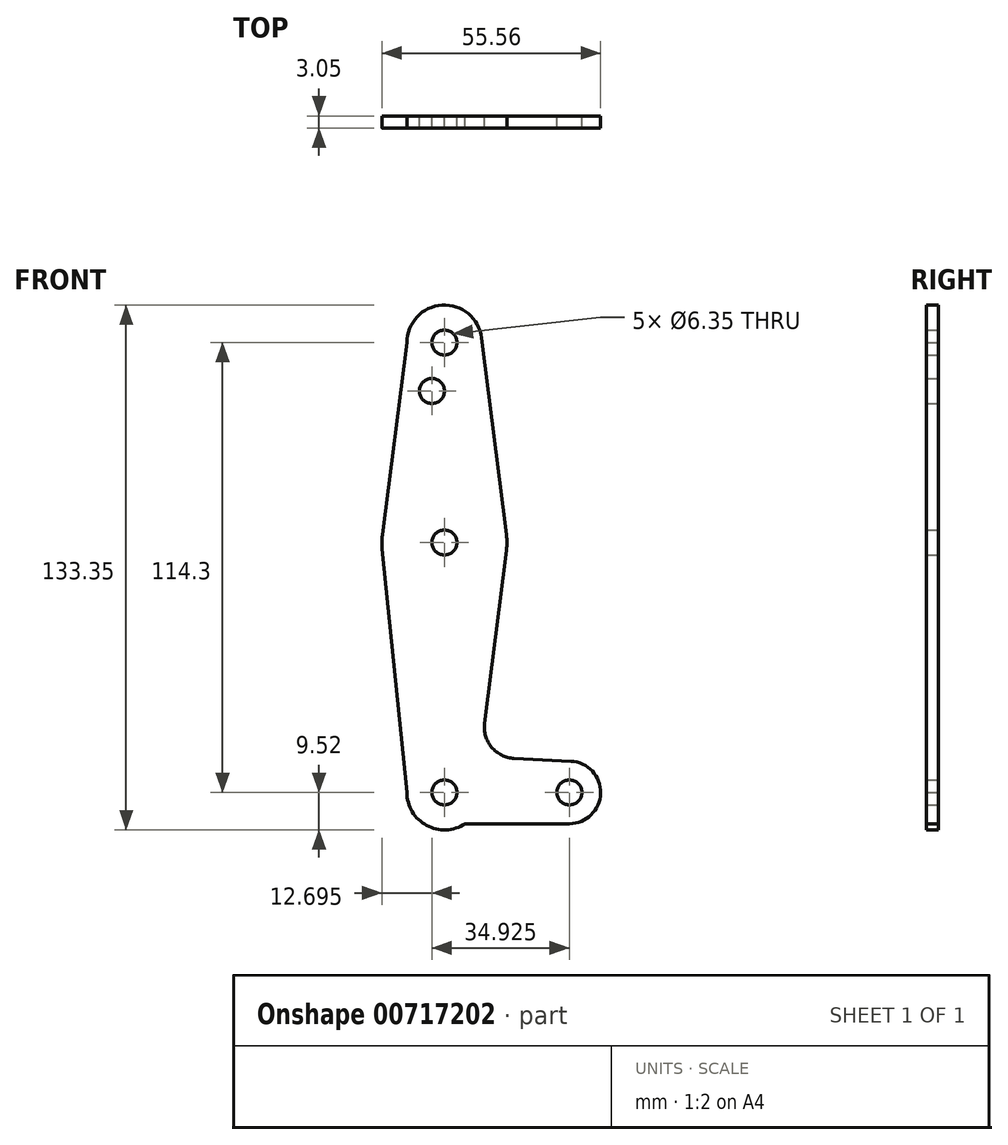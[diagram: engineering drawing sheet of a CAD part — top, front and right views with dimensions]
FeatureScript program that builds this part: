
annotation { "Feature Type Name" : "Feature", "Feature Type Description" : "" }
export const myFeature = defineFeature(function(context is Context, id is Id, definition is map)
    precondition{}
    {
        {
            var Q0;
            Q0=qCreatedBy(makeId("Front.planeOp"),FACE);
            var sketch = newSketch(context, id + "F0", { "sketchPlane" : qUnion([Q0])});
            skLineSegment(sketch, "E0", {"start": v(0, 0) * mm, "end": v(0, 114.3) * mm, "construction": true});
            skLineSegment(sketch, "E1", {"start": v(0, 0) * mm, "end": v(31.75, 0) * mm, "construction": true});
            skCircle(sketch, "E2", {"center": v(0, 114.3) * mm, "radius": 9.53 * mm});
            skCircle(sketch, "E3", {"center": v(0, 63.5) * mm, "radius": 15.88 * mm});
            skCircle(sketch, "E4", {"center": v(31.75, 0) * mm, "radius": 7.94 * mm});
            skLineSegment(sketch, "E5", {"start": v(-9.52, 114.3) * mm, "end": v(-15.75, 65.5) * mm});
            skLineSegment(sketch, "E6", {"start": v(9.45, 115.5) * mm, "end": v(15.75, 65.48) * mm});
            skCircle(sketch, "E7", {"center": v(0, 114.3) * mm, "radius": 3.18 * mm});
            skCircle(sketch, "E8", {"center": v(0, 0) * mm, "radius": 9.53 * mm});
            skLineSegment(sketch, "E9", {"start": v(-9.52, 0) * mm, "end": v(-15.8, 61.9) * mm});
            skLineSegment(sketch, "E10", {"start": v(15.75, 61.52) * mm, "end": v(10.22, 17.58) * mm});
            skLineSegment(sketch, "E11", {"start": v(32.15, 7.93) * mm, "end": v(17.7, 8.65) * mm});
            skLineSegment(sketch, "E12", {"start": v(31.75, -7.94) * mm, "end": v(5.27, -7.94) * mm});
            skCircle(sketch, "E13", {"center": v(0, 63.5) * mm, "radius": 3.18 * mm});
            skCircle(sketch, "E14", {"center": v(0, 0) * mm, "radius": 3.18 * mm});
            skCircle(sketch, "E15", {"center": v(31.75, 0) * mm, "radius": 3.18 * mm});
            skArc(sketch, "E16.filletArc", {"start": v(10.22, 17.58) * mm, "mid": v(12.01, 11.48) * mm, "end": v(17.7, 8.65) * mm});
            skCircle(sketch, "E17", {"center": v(-3.18, 102) * mm, "radius": 3.18 * mm});
            skSolve(sketch);
        }
        {
            var Q0;
            Q0 = qSketchRegion(id + "F0", true);
            extrude(context, id + "F1", {"entities" : qUnion([Q0]), "depth" : 3.05 * mm, "offsetDistance" : 25.4 * mm});
        }
    });
